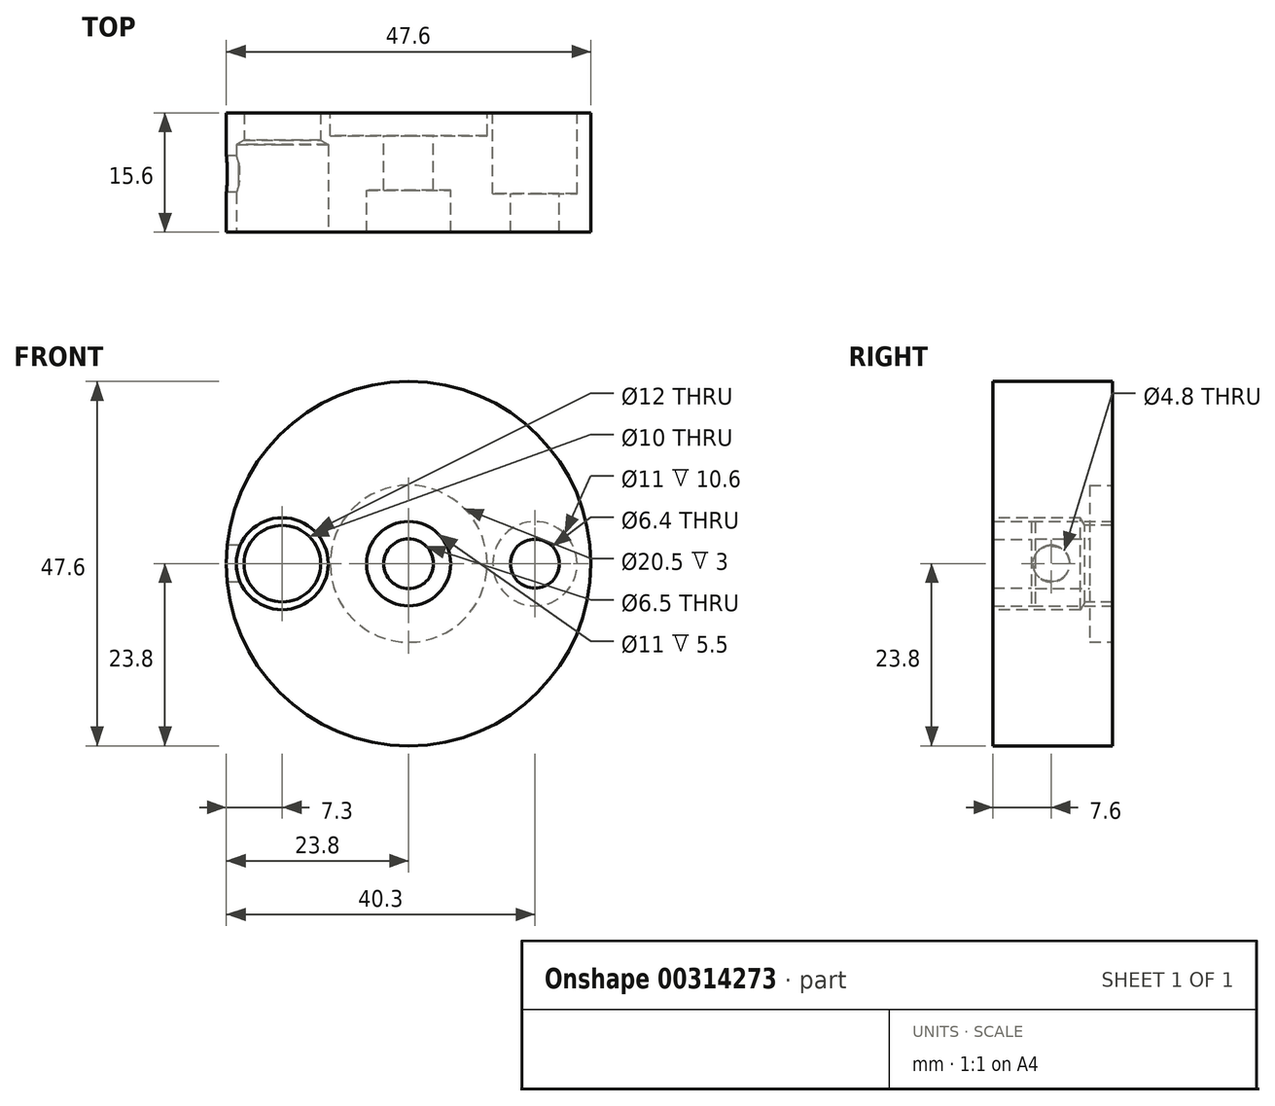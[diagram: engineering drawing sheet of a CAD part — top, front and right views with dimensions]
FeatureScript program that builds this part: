
annotation { "Feature Type Name" : "Feature", "Feature Type Description" : "" }
export const myFeature = defineFeature(function(context is Context, id is Id, definition is map)
    precondition{}
    {
        {
            var Q0;
            Q0=qCreatedBy(makeId("Front.planeOp"),FACE);
            var sketch = newSketch(context, id + "F0", { "sketchPlane" : qUnion([Q0])});
            skCircle(sketch, "E0", {"center": v(0, 0) * mm, "radius": 23.8 * mm});
            skSolve(sketch);
        }
        {
            var Q0;
            Q0=makeQuery(id+"F0.imprint","IMPRINT",FACE,{"disambiguationData":[TD([[makeQuery(id+"F0.imprint","IMPRINT",EDGE,{"derivedFrom":sQuery(id+"F0.wireOp",EDGE,"E0")}),1.0]])]});
            extrude(context, id + "F1", {"entities" : qUnion([Q0]), "depth" : 15.6 * mm});
        }
        {
            var Q0;
            Q0=makeQuery(id+"F1.opExtrude","CAP_FACE",FACE,{"disambiguationData":[OSD([sQuery(id+"F0.wireOp",EDGE,"E0")])],"isStart":false});
            var sketch = newSketch(context, id + "F2", { "sketchPlane" : qUnion([Q0])});
            skCircle(sketch, "E1", {"center": v(-16.5, 0) * mm, "radius": 6 * mm});
            skSolve(sketch);
        }
        {
            var Q0;
            Q0=makeQuery(id+"F2.imprint","IMPRINT",FACE,{"disambiguationData":[TD([[makeQuery(id+"F2.imprint","IMPRINT",EDGE,{"derivedFrom":sQuery(id+"F2.wireOp",EDGE,"E1")}),1.0]])]});
            extrude(context, id + "F3", {"entities" : qUnion([Q0]), "operationType" : NewBodyOperationType.REMOVE, "oppositeDirection" : true, "depth" : 12 * mm});
        }
        {
            var Q0;
            Q0=makeQuery(id+"F3.boolean.opBoolean","COPY",FACE,{"derivedFrom":makeQuery(id+"F3.opExtrude","CAP_FACE",FACE,{"disambiguationData":[OSD([sQuery(id+"F2.wireOp",EDGE,"E1")])],"isStart":false})});
            var sketch = newSketch(context, id + "F4", { "sketchPlane" : qUnion([Q0])});
            skCircle(sketch, "E2", {"center": v(-16.5, 0) * mm, "radius": 5 * mm});
            skSolve(sketch);
        }
        {
            var Q0;
            Q0=makeQuery(id+"F4.imprint","IMPRINT",FACE,{"disambiguationData":[TD([[makeQuery(id+"F4.imprint","IMPRINT",EDGE,{"derivedFrom":sQuery(id+"F4.wireOp",EDGE,"E2")}),1.0]])]});
            extrude(context, id + "F5", {"entities" : qUnion([Q0]), "operationType" : NewBodyOperationType.REMOVE, "oppositeDirection" : true, "depth" : 106.2 * mm});
        }
        {
            var Q0;
            Q0=makeQuery(id+"F3.boolean.opBoolean","COPY",EDGE,{"derivedFrom":makeQuery(id+"F3.opExtrude","CAP_EDGE",EDGE,{"disambiguationData":[OSD([sQuery(id+"F2.wireOp",EDGE,"E1")])],"isStart":false})});
            chamfer(context, id + "F6", {"entities" : qUnion([Q0]), "chamferType" : ChamferType.OFFSET_ANGLE, "width" : 1 * mm, "oppositeDirection" : false, "angle" : 30 * degree, "tangentPropagation" : true});
        }
        {
            var Q0;
            Q0=qCreatedBy(makeId("Top.planeOp"),FACE);
            var sketch = newSketch(context, id + "F7", { "sketchPlane" : qUnion([Q0])});
            skLineSegment(sketch, "E3", {"start": v(0, 0) * mm, "end": v(0, -44.76) * mm});
            skSolve(sketch);
        }
        {
            var Q0;
            Q0=makeQuery(id+"F1.opExtrude","CAP_FACE",FACE,{"disambiguationData":[OSD([sQuery(id+"F0.wireOp",EDGE,"E0")])],"isStart":true});
            var sketch = newSketch(context, id + "F8", { "sketchPlane" : qUnion([Q0])});
            skCircle(sketch, "E4", {"center": v(-16.5, 0) * mm, "radius": 5.5 * mm});
            skSolve(sketch);
        }
        {
            var Q0;
            Q0=makeQuery(id+"F8.imprint","IMPRINT",FACE,{"disambiguationData":[TD([[makeQuery(id+"F8.imprint","IMPRINT",EDGE,{"derivedFrom":sQuery(id+"F8.wireOp",EDGE,"E4")}),1.0]])]});
            extrude(context, id + "F9", {"entities" : qUnion([Q0]), "operationType" : NewBodyOperationType.REMOVE, "oppositeDirection" : true, "depth" : 10.6 * mm});
        }
        {
            var Q0;
            Q0=makeQuery(id+"F9.boolean.opBoolean","COPY",FACE,{"derivedFrom":makeQuery(id+"F9.opExtrude","CAP_FACE",FACE,{"disambiguationData":[OSD([sQuery(id+"F8.wireOp",EDGE,"E4")])],"isStart":false})});
            var sketch = newSketch(context, id + "F10", { "sketchPlane" : qUnion([Q0])});
            skCircle(sketch, "E5", {"center": v(-16.5, 0) * mm, "radius": 3.2 * mm});
            skSolve(sketch);
        }
        {
            var Q0;
            Q0=makeQuery(id+"F10.imprint","IMPRINT",FACE,{"disambiguationData":[TD([[makeQuery(id+"F10.imprint","IMPRINT",EDGE,{"derivedFrom":sQuery(id+"F10.wireOp",EDGE,"E5")}),1.0]])]});
            extrude(context, id + "F11", {"entities" : qUnion([Q0]), "operationType" : NewBodyOperationType.REMOVE, "oppositeDirection" : true, "depth" : 23.7 * mm});
        }
        {
            var Q0;
            Q0=qCreatedBy(makeId("Top.planeOp"),FACE);
            var sketch = newSketch(context, id + "F12", { "sketchPlane" : qUnion([Q0])});
            skLineSegment(sketch, "E6", {"start": v(0, 0) * mm, "end": v(0, -44.63) * mm});
            skSolve(sketch);
        }
        {
            var Q0;
            Q0=makeQuery(id+"F1.opExtrude","CAP_FACE",FACE,{"disambiguationData":[OSD([sQuery(id+"F0.wireOp",EDGE,"E0")])],"isStart":true});
            var sketch = newSketch(context, id + "F13", { "sketchPlane" : qUnion([Q0])});
            skCircle(sketch, "E7", {"center": v(0, 0) * mm, "radius": 10.25 * mm});
            skSolve(sketch);
        }
        {
            var Q0;
            Q0=makeQuery(id+"F13.imprint","IMPRINT",FACE,{"disambiguationData":[TD([[makeQuery(id+"F13.imprint","IMPRINT",EDGE,{"derivedFrom":sQuery(id+"F13.wireOp",EDGE,"E7")}),1.0]])]});
            extrude(context, id + "F14", {"entities" : qUnion([Q0]), "operationType" : NewBodyOperationType.REMOVE, "oppositeDirection" : true, "depth" : 3 * mm});
        }
        {
            var Q0;
            Q0=makeQuery(id+"F14.boolean.opBoolean","COPY",FACE,{"derivedFrom":makeQuery(id+"F14.opExtrude","CAP_FACE",FACE,{"disambiguationData":[OSD([sQuery(id+"F13.wireOp",EDGE,"E7")])],"isStart":false})});
            var sketch = newSketch(context, id + "F15", { "sketchPlane" : qUnion([Q0])});
            skCircle(sketch, "E8", {"center": v(0, 0) * mm, "radius": 3.25 * mm});
            skSolve(sketch);
        }
        {
            var Q0;
            Q0 = qSketchRegion(id + "F15", true);
            extrude(context, id + "F16", {"entities" : qUnion([Q0]), "operationType" : NewBodyOperationType.REMOVE, "oppositeDirection" : true, "depth" : 7.1 * mm});
        }
        {
            var Q0;
            Q0=makeQuery(id+"F16.boolean.opBoolean","COPY",FACE,{"derivedFrom":makeQuery(id+"F16.opExtrude","CAP_FACE",FACE,{"disambiguationData":[OSD([sQuery(id+"F15.wireOp",EDGE,"E8")])],"isStart":false})});
            var sketch = newSketch(context, id + "F17", { "sketchPlane" : qUnion([Q0])});
            skCircle(sketch, "E9", {"center": v(0, 0) * mm, "radius": 5.5 * mm});
            skSolve(sketch);
        }
        {
            var Q0;
            Q0 = qSketchRegion(id + "F17", true);
            extrude(context, id + "F18", {"entities" : qUnion([Q0]), "operationType" : NewBodyOperationType.REMOVE, "oppositeDirection" : true, "depth" : 37.6 * mm});
        }
        {
            var Q0;
            Q0=qCreatedBy(makeId("Right.planeOp"),FACE);
            cPlane(context, id + "F19", {"entities" : qUnion([Q0]), "cplaneType" : CPlaneType.OFFSET, "offset" : 23.8 * mm, "oppositeDirection" : true, "width" : 150 * mm, "height" : 150 * mm});
        }
        {
            var Q0;
            Q0=qCreatedBy(id+"F19.planeOp",FACE);
            var sketch = newSketch(context, id + "F20", { "sketchPlane" : qUnion([Q0])});
            skCircle(sketch, "E10", {"center": v(-8, 0) * mm, "radius": 2.4 * mm});
            skSolve(sketch);
        }
        {
            var Q0;
            Q0=sQuery(id+"F20.wireOp",VERTEX,"E10.center");
            var Q1;
            Q1=makeQuery(id+"F1.opExtrude","SWEPT_BODY",BODY,{"disambiguationData":[OSD([sQuery(id+"F0.wireOp",EDGE,"E0")])]});
            hole(context, id + "F21", {"style" : HoleStyle.SIMPLE, "endStyle" : HoleEndStyle.BLIND, "oppositeDirection" : true, "holeDiameter" : 4.8 * mm, "holeDepth" : 1.5 * mm, "tappedDepth" : 12 * mm, "tapClearance" : 3, "locations" : qUnion([Q0]), "scope" : qUnion([Q1])});
        }
    });
